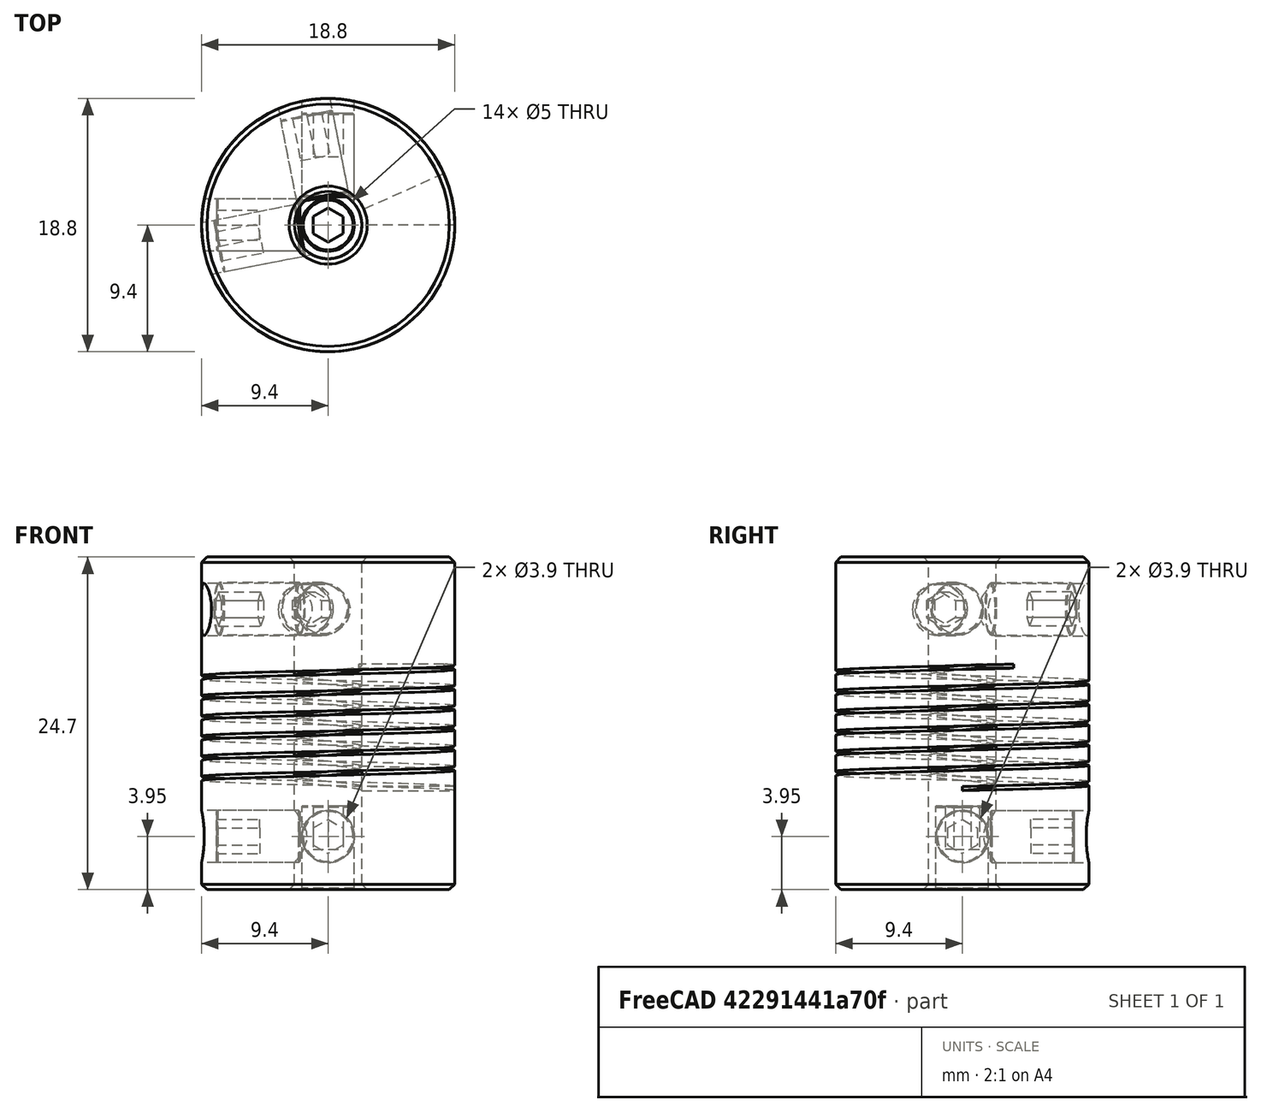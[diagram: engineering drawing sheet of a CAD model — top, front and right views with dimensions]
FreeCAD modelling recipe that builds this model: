
FCSTD DOCUMENT  (FreeCAD 0.14R3702 (Git))
Label: z-coupling
License: CC-BY 3.0
LicenseURL: http://creativecommons.org/licenses/by/3.0/
objects: Part::Cylinder×7, Part::Feature×5, Part::Cut×3, Sketcher::SketchObject×2, PartDesign::Chamfer×2, App::DocumentObjectGroup×2, Part::Helix×1, Part::Sweep×1, Part::MultiFuse×1, PartDesign::Pocket×1, Part::Chamfer×1, Part::Compound×1
note: 26 computed .brp shape members not serialized (recipe doc carries the construction recipe); baked Part::Feature solids carry a one-line shape summary decoded from their .brp

FEATURE [Part::Cylinder] Cylinder  label="main-body"
  Angle = 360
  Height = 24.7
  Radius = 9.4
FEATURE [Part::Helix] Helix  label="thread-path"
  Angle = 0
  Height = 9.1
  LocalCoord = 0
  Pitch = 1.5
  Radius = 10
  Style = 1
FEATURE [Sketcher::SketchObject] Sketch  label="thread-section-sketch"
  Placement = pos=(0,0,0) rot=(-1,0,0;4.71239rad)
  sketch-geometry (4):
    g0: LineSegment StartX=0 StartY=0 StartZ=0 EndX=10 EndY=0 EndZ=0
    g1: LineSegment StartX=10 StartY=0 StartZ=0 EndX=10 EndY=0.3 EndZ=0
    g2: LineSegment StartX=10 StartY=0.3 StartZ=0 EndX=0 EndY=0.3 EndZ=0
    g3: LineSegment StartX=0 StartY=0.3 StartZ=0 EndX=0 EndY=0 EndZ=0
  constraints (11):
    c: Coincident(g0,g1)
    c: Coincident(g1,g2)
    c: Coincident(g2,g3)
    c: Coincident(g3,g0)
    c: Horizontal(g0)
    c: Horizontal(g2)
    c: Vertical(g1)
    c: Vertical(g3)
    c: Coincident(g0,g-1)
    c: DistanceX(g2) = -10
    c: DistanceY(g1) = 0.3
FEATURE [Part::Sweep] Sweep  label="flexible-part-male"
  Frenet = true
  Placement = pos=(0,0,7.35) rot=(0,0,1;0rad)
  Sections = -> [Sketch]
  Solid = true
  Spine = -> Helix [Edge1]
  Transition = 1
FEATURE [Part::Cut] Cut  label="main-body-flexible-part"
  Base = -> Cylinder
  Tool = -> Sweep
FEATURE [Part::Cylinder] Cylinder001  label="vertical-drill-cylinder"
  Angle = 360
  Height = 30
  Placement = pos=(0,0,-3) rot=(0,0,1;0rad)
  Radius = 2.5
FEATURE [Part::Cut] Cut001  label="vertical-drill"
  Base = -> Cut
  Tool = -> Cylinder001
FEATURE [Part::Cylinder] Cylinder002  label="bottom-setscrew-1-cylinder"
  Angle = 360
  Height = 15
  Placement = pos=(0,0,3.95) rot=(1,0,0;1.5708rad)
  Radius = 1.95
FEATURE [Part::Cylinder] Cylinder003  label="bottom-setscrew-2-cylinder"
  Angle = 360
  Height = 15
  Placement = pos=(0,0,3.95) rot=(0.57735,0.57735,0.57735;2.0944rad)
  Radius = 1.95
FEATURE [Part::Cylinder] Cylinder004  label="top-setscrew-1-cylinder001"
  Angle = 360
  Height = 15
  Placement = pos=(0,0,20.8) rot=(0.990855,0.095409,0.095409;1.57998rad)
  Radius = 1.95
FEATURE [Part::Cylinder] Cylinder005  label="top-setscrew-2-cylinder001"
  Angle = 360
  Height = 15
  Placement = pos=(0,0,20.8) rot=(0.503588,0.610901,0.610901;2.20857rad)
  Radius = 1.95
FEATURE [Part::MultiFuse] Fusion  label="setscrew-cylinders"
  Placement = pos=(0,0,0) rot=(0,0,1;3.14159rad)
  Shapes = -> [Cylinder002,Cylinder005,Cylinder004,Cylinder003]
FEATURE [Part::Cut] Cut002  label="horizontal-drills"
  Base = -> Cut001
  Tool = -> Fusion
FEATURE [Part::Cylinder] Cylinder006  label="setscrew-body"
  Angle = 360
  Height = 6.2
  Radius = 1.95
FEATURE [Sketcher::SketchObject] Sketch001  label="hexa-sketch"
  Placement = pos=(0,0,6.2) rot=(0,0,1;0rad)
  Support = -> Cylinder006 [Face2]
  sketch-geometry (8):
    g0: LineSegment StartX=-1.1 StartY=-0.635085 StartZ=0 EndX=-1.1 EndY=0.635085 EndZ=0
    g1: LineSegment StartX=-1.1 StartY=0.635085 StartZ=0 EndX=0 EndY=1.27017 EndZ=0
    g2: LineSegment [constr] StartX=-1.1 StartY=0.635085 StartZ=0 EndX=0 EndY=0 EndZ=0
    g3: LineSegment [constr] StartX=0 StartY=1.27017 StartZ=0 EndX=0 EndY=0 EndZ=0
    g4: LineSegment StartX=-1.1 StartY=-0.635085 StartZ=0 EndX=0 EndY=-1.27017 EndZ=0
    g5: LineSegment StartX=0 StartY=-1.27017 StartZ=0 EndX=1.1 EndY=-0.635085 EndZ=0
    g6: LineSegment StartX=1.1 StartY=-0.635085 StartZ=0 EndX=1.1 EndY=0.635085 EndZ=0
    g7: LineSegment StartX=1.1 StartY=0.635085 StartZ=0 EndX=0 EndY=1.27017 EndZ=0
  constraints (21):
    c: Vertical(g0)
    c: Coincident(g0,g1)
    c: Symmetric(g0,g0,g-1)
    c: Coincident(g2,g-1)
    c: Coincident(g2,g0)
    c: Angle(g-2,g2) = 1.0472
    c: Vertical(g3)
    c: Coincident(g3,g-1)
    c: Coincident(g3,g1)
    c: Equal(g3,g2)
    c: Coincident(g0,g4)
    c: PointOnObject(g4,g-2)
    c: Coincident(g4,g5)
    c: Coincident(g5,g6)
    c: Vertical(g6)
    c: Coincident(g6,g7)
    c: Coincident(g7,g1)
    c: Symmetric(g5,g6,g-1)
    c: Symmetric(g0,g6,g-2)
    c: Symmetric(g4,g1,g-1)
    c: DistanceX(g0,g6) = 2.2
FEATURE [PartDesign::Pocket] Pocket  label="hexa"
  Length = 3.2
  Sketch = -> Sketch001
  Type = 0
FEATURE [PartDesign::Chamfer] Chamfer001
  Base = -> Pocket [Edge3]
  Size = 0.1
FEATURE [PartDesign::Chamfer] Chamfer002
  Base = -> Chamfer001 [Edge3]
  Size = 0.1
FEATURE [App::DocumentObjectGroup] Group  label="setscrew-src"
  Group = -> [Cylinder006,Pocket,Chamfer001,Chamfer002]
FEATURE [Part::Chamfer] Chamfer003
  Base = -> Cut002
  Edges = 4 edges r=0.4: [Edge7,Edge41,Edge63,Edge68]
FEATURE [App::DocumentObjectGroup] Group001  label="coupling-src"
  Group = -> [Chamfer003,Helix]
FEATURE [Part::Feature] Chamfer  label="coupling-final"
  shape: bbox 28.44 x 28.71 x 24.7 mm, 28 faces (baked)
FEATURE [Part::Feature] Chamfer004  label="setscrew-bottom-1"
  Placement = pos=(0,2.09552,3.95) rot=(-1,0,0;1.5708rad)
  shape: bbox 3.9 x 6.2 x 3.9 mm, 12 faces (baked)
FEATURE [Part::Feature] Chamfer005  label="setscrew-bottom-002"
  Placement = pos=(-2.09552,0,3.95) rot=(-0.57735,-0.57735,0.57735;2.0944rad)
  shape: bbox 6.2 x 3.9 x 3.9 mm, 12 faces (baked)
FEATURE [Part::Feature] Chamfer006  label="setscrew-top-1"
  Placement = pos=(-0.399844,2.05702,20.85) rot=(-0.990855,-0.095409,0.095409;1.57998rad)
  shape: bbox 4.973 x 6.792 x 3.9 mm, 12 faces (baked)
FEATURE [Part::Feature] Chamfer007  label="setscrew-top-2"
  Placement = pos=(-2.05702,-0.399844,20.85) rot=(-0.503588,-0.610901,0.610901;2.20857rad)
  shape: bbox 6.792 x 4.973 x 3.9 mm, 12 faces (baked)
FEATURE [Part::Compound] Compound  label="coupling-compound"
  Links = -> [Chamfer,Chamfer004,Chamfer005,Chamfer006,Chamfer007]
